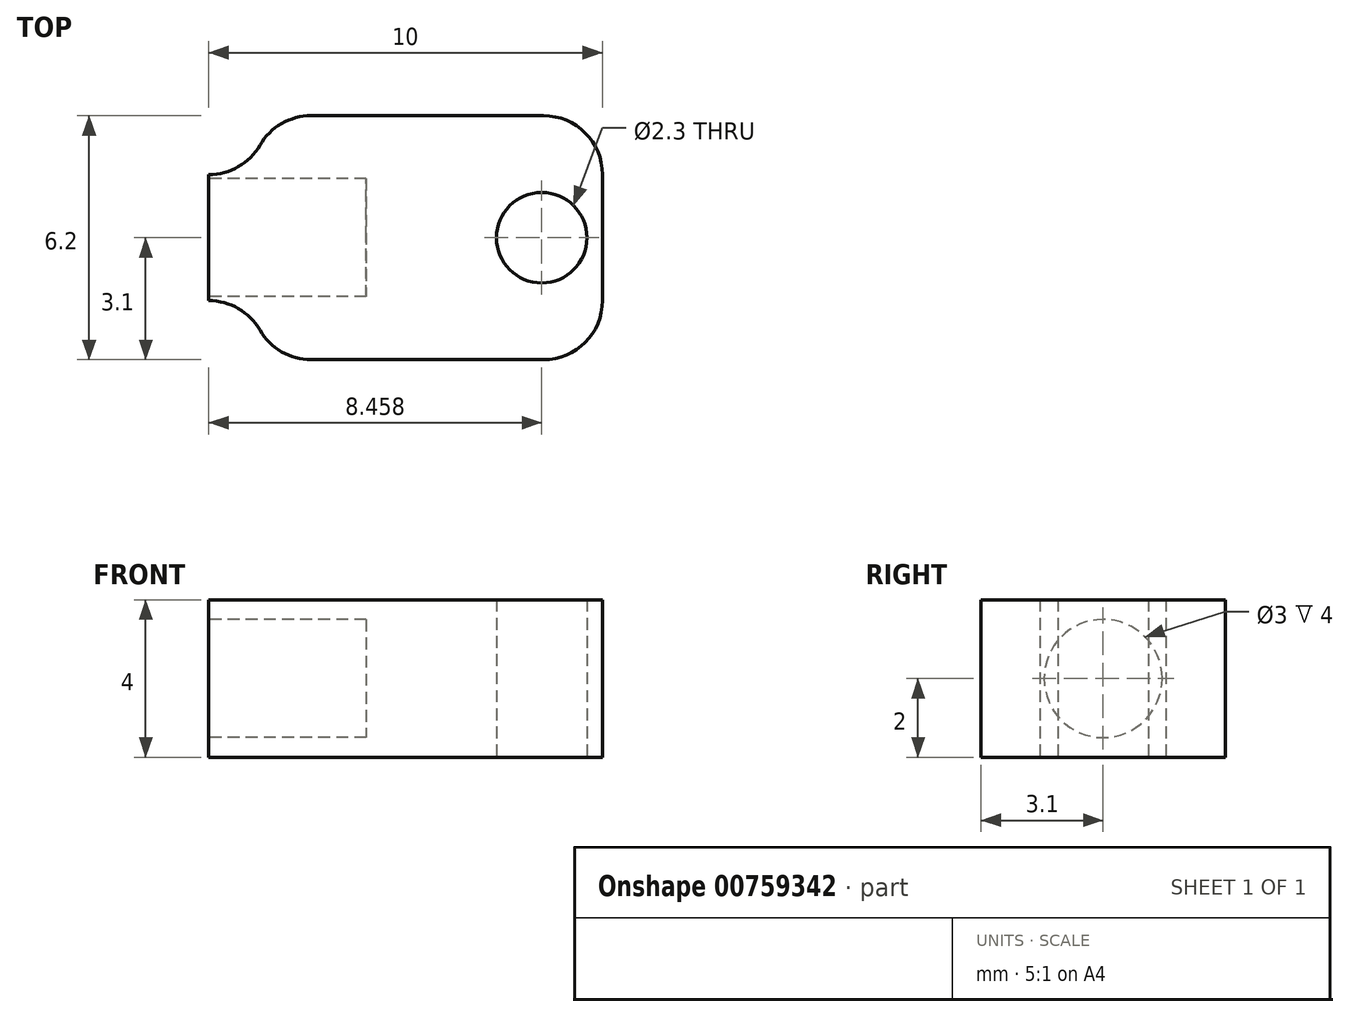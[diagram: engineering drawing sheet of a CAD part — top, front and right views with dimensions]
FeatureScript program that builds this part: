
annotation { "Feature Type Name" : "Feature", "Feature Type Description" : "" }
export const myFeature = defineFeature(function(context is Context, id is Id, definition is map)
    precondition{}
    {
        {
            var Q0;
            Q0=qCreatedBy(makeId("Top.planeOp"),FACE);
            var sketch = newSketch(context, id + "F0", { "sketchPlane" : qUnion([Q0])});
            skLineSegment(sketch, "E0.bottom", {"start": v(-3.5, 3.1) * mm, "end": v(3.5, 3.1) * mm});
            skLineSegment(sketch, "E0.top", {"start": v(-3.5, -3.1) * mm, "end": v(3.5, -3.1) * mm});
            skLineSegment(sketch, "E0.left", {"start": v(-5, 1.6) * mm, "end": v(-5, -1.6) * mm});
            skLineSegment(sketch, "E0.right", {"start": v(5, 1.6) * mm, "end": v(5, -1.6) * mm});
            skPoint(sketch, "E0.middle", {"position": v(0, 0) * mm});
            skCircle(sketch, "E1", {"center": v(3.46, 0) * mm, "radius": 1.15 * mm});
            skPoint(sketch, "E2.visualSharp", {"position": v(5, -3.1) * mm});
            skArc(sketch, "E2.filletArc", {"start": v(3.5, -3.1) * mm, "mid": v(4.56, -2.66) * mm, "end": v(5, -1.6) * mm});
            skPoint(sketch, "E3.visualSharp", {"position": v(5, 3.1) * mm});
            skArc(sketch, "E3.filletArc", {"start": v(5, 1.6) * mm, "mid": v(4.56, 2.66) * mm, "end": v(3.5, 3.1) * mm});
            skArc(sketch, "E4", {"start": v(-5, -1.6) * mm, "mid": v(-3.94, -2.04) * mm, "end": v(-3.5, -3.1) * mm});
            skArc(sketch, "E5", {"start": v(-5, 1.6) * mm, "mid": v(-3.94, 2.04) * mm, "end": v(-3.5, 3.1) * mm});
            skSolve(sketch);
        }
        {
            var Q0;
            Q0 = qSketchRegion(id + "F0", true);
            extrude(context, id + "F1", {"entities" : qUnion([Q0]), "depth" : 4 * mm, "offsetDistance" : 25 * mm});
        }
        {
            var Q0;
            Q0=makeQuery(id+"F1.opExtrude","SWEPT_EDGE",EDGE,{"disambiguationData":[OSD([sQuery(id+"F0.wireOp",EDGE,"E0.top"),sQuery(id+"F0.wireOp",EDGE,"E4")])]});
            var Q1;
            Q1=makeQuery(id+"F1.opExtrude","SWEPT_EDGE",EDGE,{"disambiguationData":[OSD([sQuery(id+"F0.wireOp",EDGE,"E0.bottom"),sQuery(id+"F0.wireOp",EDGE,"E5")])]});
            fillet(context, id + "F2", {"entities" : qUnion([Q0, Q1]), "radius" : 1.5 * mm, "tangentPropagation" : true, "allowEdgeOverflow" : false});
        }
        {
            var Q0;
            Q0=makeQuery(id+"F1.opExtrude","SWEPT_FACE",FACE,{"disambiguationData":[OSD([sQuery(id+"F0.wireOp",EDGE,"E0.left")])]});
            var sketch = newSketch(context, id + "F3", { "sketchPlane" : qUnion([Q0])});
            skCircle(sketch, "E6", {"center": v(0, 2) * mm, "radius": 1.5 * mm});
            skPoint(sketch, "E6.centerSnap0", {"position": v(-1.6, 2) * mm});
            skSolve(sketch);
        }
        {
            var Q0;
            Q0=makeQuery(id+"F3.imprint","IMPRINT",FACE,{"disambiguationData":[TD([[makeQuery(id+"F3.imprint","IMPRINT",EDGE,{"derivedFrom":sQuery(id+"F3.wireOp",EDGE,"E6")}),1.0]])]});
            extrude(context, id + "F4", {"entities" : qUnion([Q0]), "operationType" : NewBodyOperationType.REMOVE, "oppositeDirection" : true, "depth" : 4 * mm, "offsetDistance" : 25 * mm});
        }
    });
